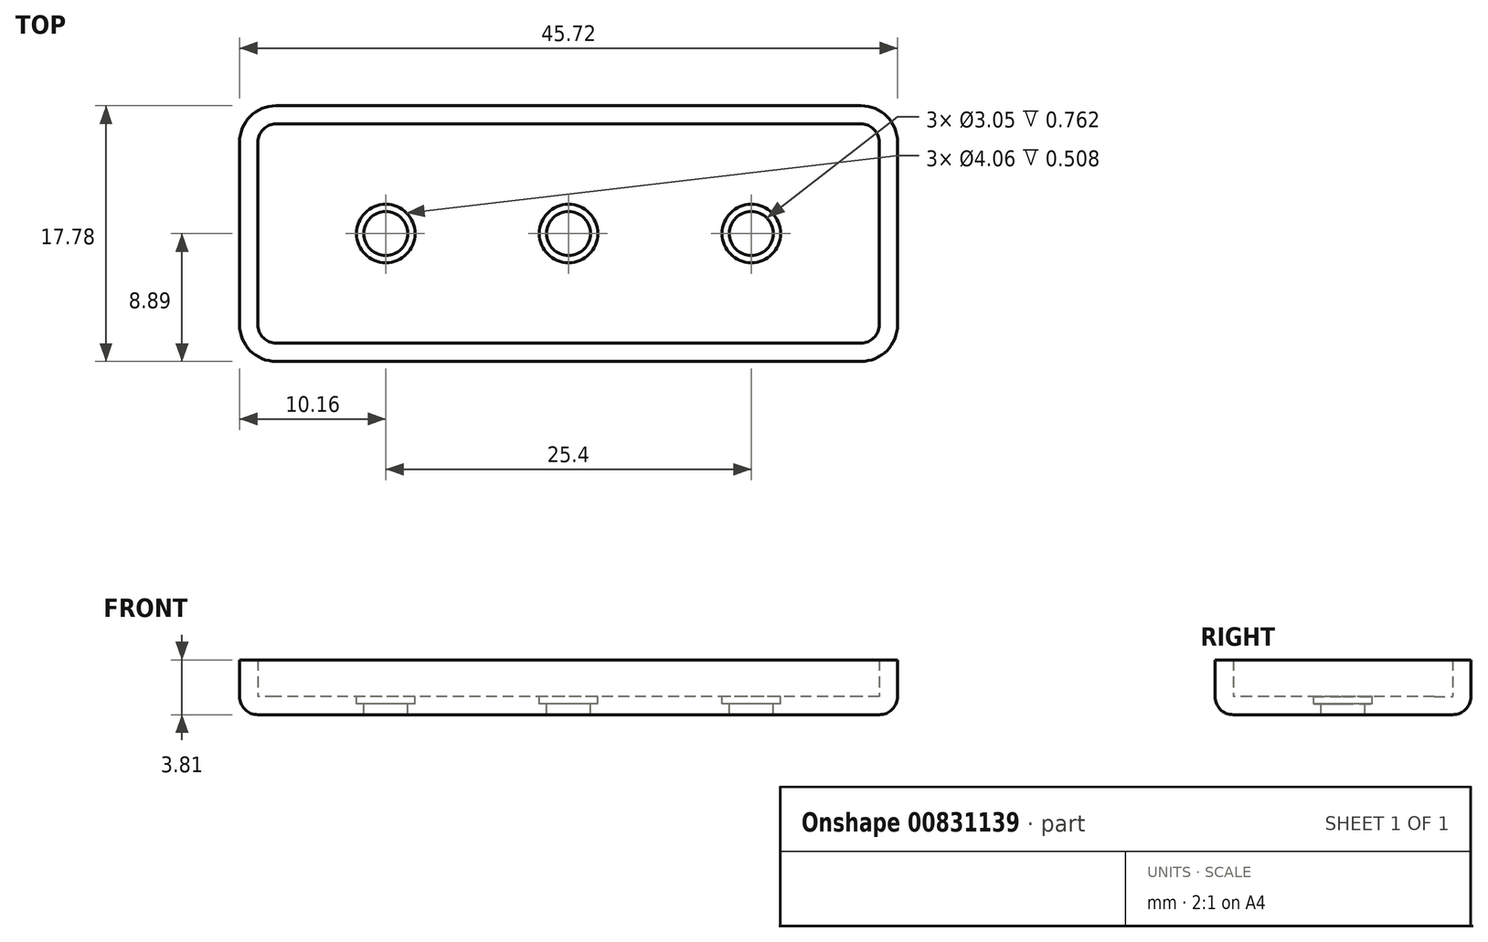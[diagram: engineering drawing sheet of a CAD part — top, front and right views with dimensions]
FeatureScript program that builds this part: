
annotation { "Feature Type Name" : "Feature", "Feature Type Description" : "" }
export const myFeature = defineFeature(function(context is Context, id is Id, definition is map)
    precondition{}
    {
        {
            var Q0;
            Q0=qCreatedBy(makeId("Top.planeOp"),FACE);
            var sketch = newSketch(context, id + "F0", { "sketchPlane" : qUnion([Q0])});
            skLineSegment(sketch, "E0.bottom", {"start": v(20.32, 8.9) * mm, "end": v(-20.32, 8.9) * mm});
            skLineSegment(sketch, "E0.top", {"start": v(20.32, -8.9) * mm, "end": v(-20.32, -8.9) * mm});
            skLineSegment(sketch, "E0.left", {"start": v(22.86, 6.35) * mm, "end": v(22.86, -6.35) * mm});
            skLineSegment(sketch, "E0.right", {"start": v(-22.86, 6.35) * mm, "end": v(-22.86, -6.35) * mm});
            skPoint(sketch, "E0.middle", {"position": v(0, 0) * mm});
            skPoint(sketch, "E1.visualSharp", {"position": v(-22.86, 8.9) * mm});
            skArc(sketch, "E1.filletArc", {"start": v(-20.32, 8.9) * mm, "mid": v(-22.12, 8.15) * mm, "end": v(-22.86, 6.35) * mm});
            skPoint(sketch, "E2.visualSharp", {"position": v(22.86, 8.9) * mm});
            skArc(sketch, "E2.filletArc", {"start": v(22.86, 6.35) * mm, "mid": v(22.12, 8.15) * mm, "end": v(20.32, 8.9) * mm});
            skPoint(sketch, "E3.visualSharp", {"position": v(22.86, -8.9) * mm});
            skArc(sketch, "E3.filletArc", {"start": v(20.32, -8.9) * mm, "mid": v(22.12, -8.15) * mm, "end": v(22.86, -6.35) * mm});
            skPoint(sketch, "E4.visualSharp", {"position": v(-22.86, -8.9) * mm});
            skArc(sketch, "E4.filletArc", {"start": v(-22.86, -6.35) * mm, "mid": v(-22.12, -8.15) * mm, "end": v(-20.32, -8.9) * mm});
            skSolve(sketch);
        }
        {
            var Q0;
            Q0=qSketchRegion(id+"F0",true);
            extrude(context, id + "F1", {"entities" : qUnion([Q0]), "depth" : 3.8 * mm, "offsetDistance" : 25.4 * mm});
        }
        {
            var Q0;
            Q0=makeQuery(id+"F1.opExtrude","CAP_FACE",FACE,{"disambiguationData":[OSD([sQuery(id+"F0.wireOp",EDGE,"E0.bottom"),sQuery(id+"F0.wireOp",EDGE,"E0.top"),sQuery(id+"F0.wireOp",EDGE,"E0.left"),sQuery(id+"F0.wireOp",EDGE,"E0.right"),sQuery(id+"F0.wireOp",EDGE,"E1.filletArc"),sQuery(id+"F0.wireOp",EDGE,"E2.filletArc"),sQuery(id+"F0.wireOp",EDGE,"E3.filletArc"),sQuery(id+"F0.wireOp",EDGE,"E4.filletArc")])],"isStart":false});
            shell(context, id + "F2", {"entities" : qUnion([Q0]), "thickness" : 1.27 * mm});
        }
        {
            var Q0;
            Q0=makeQuery(id+"F2.opShell","OFFSET_FACE",FACE,{"disambiguationData":[OSD([sQuery(id+"F0.wireOp",EDGE,"E0.bottom"),sQuery(id+"F0.wireOp",EDGE,"E0.top"),sQuery(id+"F0.wireOp",EDGE,"E0.left"),sQuery(id+"F0.wireOp",EDGE,"E0.right"),sQuery(id+"F0.wireOp",EDGE,"E1.filletArc"),sQuery(id+"F0.wireOp",EDGE,"E2.filletArc"),sQuery(id+"F0.wireOp",EDGE,"E3.filletArc"),sQuery(id+"F0.wireOp",EDGE,"E4.filletArc")])]});
            var sketch = newSketch(context, id + "F3", { "sketchPlane" : qUnion([Q0])});
            skCircle(sketch, "E5", {"center": v(-12.7, 0) * mm, "radius": 1.52 * mm});
            skCircle(sketch, "E6.0.2.0", {"center": v(-12.7, 50.8) * mm, "radius": 1.52 * mm});
            skCircle(sketch, "E6.1.0.0", {"center": v(0, 0) * mm, "radius": 1.52 * mm});
            skCircle(sketch, "E6.1.2.0", {"center": v(0, 50.8) * mm, "radius": 1.52 * mm});
            skCircle(sketch, "E6.2.0.0", {"center": v(12.7, 0) * mm, "radius": 1.52 * mm});
            skCircle(sketch, "E6.2.2.0", {"center": v(12.7, 50.8) * mm, "radius": 1.52 * mm});
            skLineSegment(sketch, "E6.direction1", {"start": v(-12.7, 0) * mm, "end": v(0, 0) * mm, "construction": true});
            skLineSegment(sketch, "E6.direction2", {"start": v(-12.7, 0) * mm, "end": v(-12.7, 25.4) * mm, "construction": true});
            skSolve(sketch);
        }
        {
            var Q0;
            Q0=qSketchRegion(id+"F3",true);
            extrude(context, id + "F4", {"entities" : qUnion([Q0]), "operationType" : NewBodyOperationType.REMOVE, "oppositeDirection" : true, "depth" : 25.4 * mm, "offsetDistance" : 25.4 * mm});
        }
        {
            var Q0;
            Q0=makeQuery(id+"F2.opShell","OFFSET_FACE",FACE,{"disambiguationData":[OSD([sQuery(id+"F0.wireOp",EDGE,"E0.bottom"),sQuery(id+"F0.wireOp",EDGE,"E0.top"),sQuery(id+"F0.wireOp",EDGE,"E0.left"),sQuery(id+"F0.wireOp",EDGE,"E0.right"),sQuery(id+"F0.wireOp",EDGE,"E1.filletArc"),sQuery(id+"F0.wireOp",EDGE,"E2.filletArc"),sQuery(id+"F0.wireOp",EDGE,"E3.filletArc"),sQuery(id+"F0.wireOp",EDGE,"E4.filletArc")])]});
            var sketch = newSketch(context, id + "F5", { "sketchPlane" : qUnion([Q0])});
            skCircle(sketch, "E7", {"center": v(-12.7, 0) * mm, "radius": 2.03 * mm});
            skCircle(sketch, "E8", {"center": v(0, 0) * mm, "radius": 2.03 * mm});
            skCircle(sketch, "E9", {"center": v(12.7, 0) * mm, "radius": 2.03 * mm});
            skSolve(sketch);
        }
        {
            var Q0;
            Q0=qSketchRegion(id+"F5",true);
            extrude(context, id + "F6", {"entities" : qUnion([Q0]), "operationType" : NewBodyOperationType.REMOVE, "oppositeDirection" : true, "depth" : 0.5 * mm, "offsetDistance" : 25.4 * mm});
        }
        {
            var Q0;
            Q0=makeQuery(id+"F1.opExtrude","CAP_EDGE",EDGE,{"disambiguationData":[OSD([sQuery(id+"F0.wireOp",EDGE,"E0.top")])],"isStart":true});
            fillet(context, id + "F7", {"entities" : qUnion([Q0]), "radius" : 1.27 * mm, "tangentPropagation" : true, "allowEdgeOverflow" : false});
        }
    });
